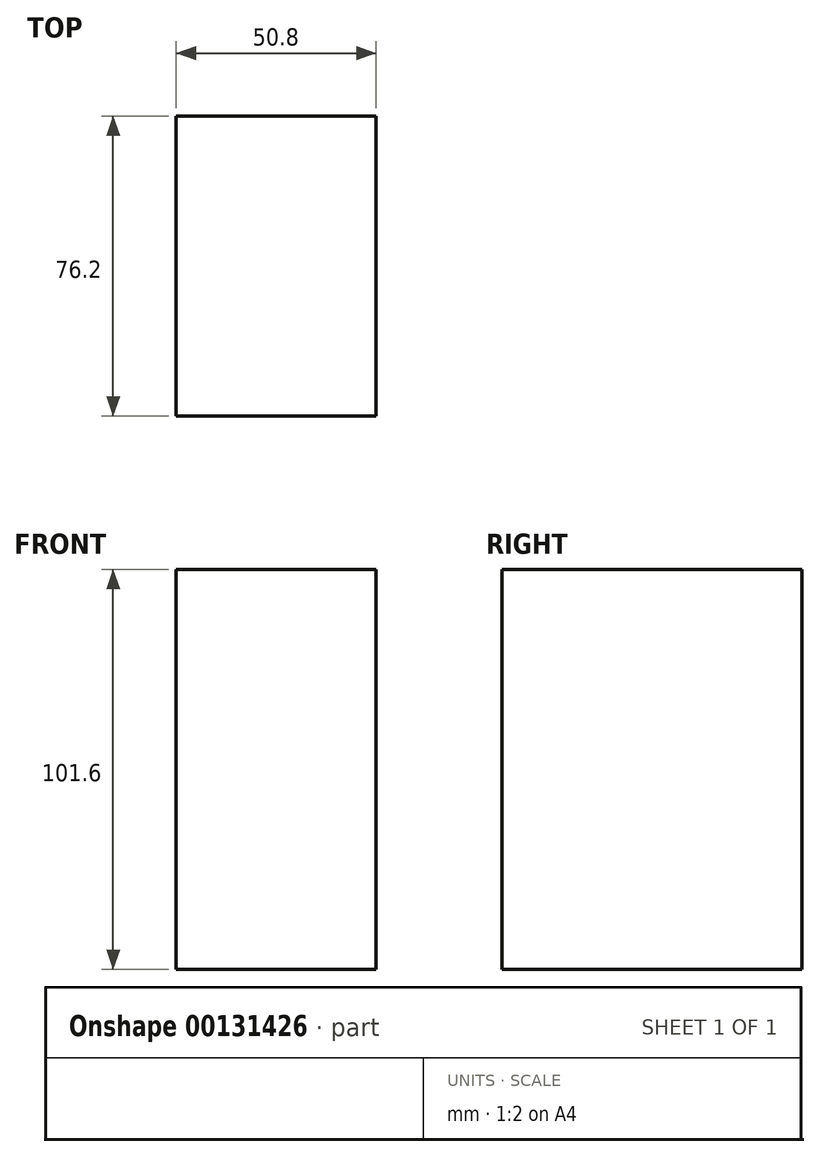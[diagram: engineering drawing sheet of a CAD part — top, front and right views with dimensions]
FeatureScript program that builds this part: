
annotation { "Feature Type Name" : "Feature", "Feature Type Description" : "" }
export const myFeature = defineFeature(function(context is Context, id is Id, definition is map)
    precondition{}
    {
        {
            var Q0;
            Q0=qCreatedBy(makeId("Front.planeOp"),FACE);
            var sketch = newSketch(context, id + "F0", { "sketchPlane" : qUnion([Q0])});
            skLineSegment(sketch, "E0.bottom", {"start": v(25.4, -50.8) * mm, "end": v(-25.4, -50.8) * mm});
            skLineSegment(sketch, "E0.top", {"start": v(25.4, 50.8) * mm, "end": v(-25.4, 50.8) * mm});
            skLineSegment(sketch, "E0.left", {"start": v(25.4, -50.8) * mm, "end": v(25.4, 50.8) * mm});
            skLineSegment(sketch, "E0.right", {"start": v(-25.4, -50.8) * mm, "end": v(-25.4, 50.8) * mm});
            skPoint(sketch, "E0.middle", {"position": v(0, 0) * mm});
            skSolve(sketch);
        }
        {
            var Q0;
            Q0 = qSketchRegion(id + "F0", true);
            extrude(context, id + "F1", {"entities" : qUnion([Q0]), "endBound" : BoundingType.SYMMETRIC, "depth" : 76.2 * mm});
        }
    });
